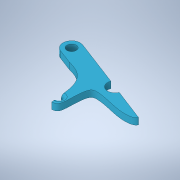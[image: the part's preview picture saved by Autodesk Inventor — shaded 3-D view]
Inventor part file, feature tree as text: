
AUTODESK INVENTOR PART (.ipt)
format: ipt  version: 2020.1 (Build 241239000, 239)  size: 171,008 bytes
history: native  units: mm
features: plane x2, sketch x2, extrude x1, fillet x1
ambient origin geometry x8: Origin, YZ Plane, XZ Plane, XY Plane, X Axis, Y Axis, Z Axis, Center Point
bodies: Solid1 (feature_tree)
feature tree (6):
  extrude  "Extrusion1"  Depth=26.3586mm
  fillet  "Fillet3"  Radius=4.0mm
  plane  "Work Plane1"
  plane  "Work Plane2"
  sketch  "Sketch3"  dims[d4=43.535mm d5=4.0mm d6=20.5358mm d7=7.0mm d9=1.5mm d10=1.2mm d13=3.0mm d14=0.0mm d21=17.25mm d22=2.6mm d23=20.507619mm d24=4.3mm d39=1.5mm d40=90.0deg]
  sketch  "Sketch1"  dims[d1=7.0mm d2=26.3586mm d3=4.0mm]
